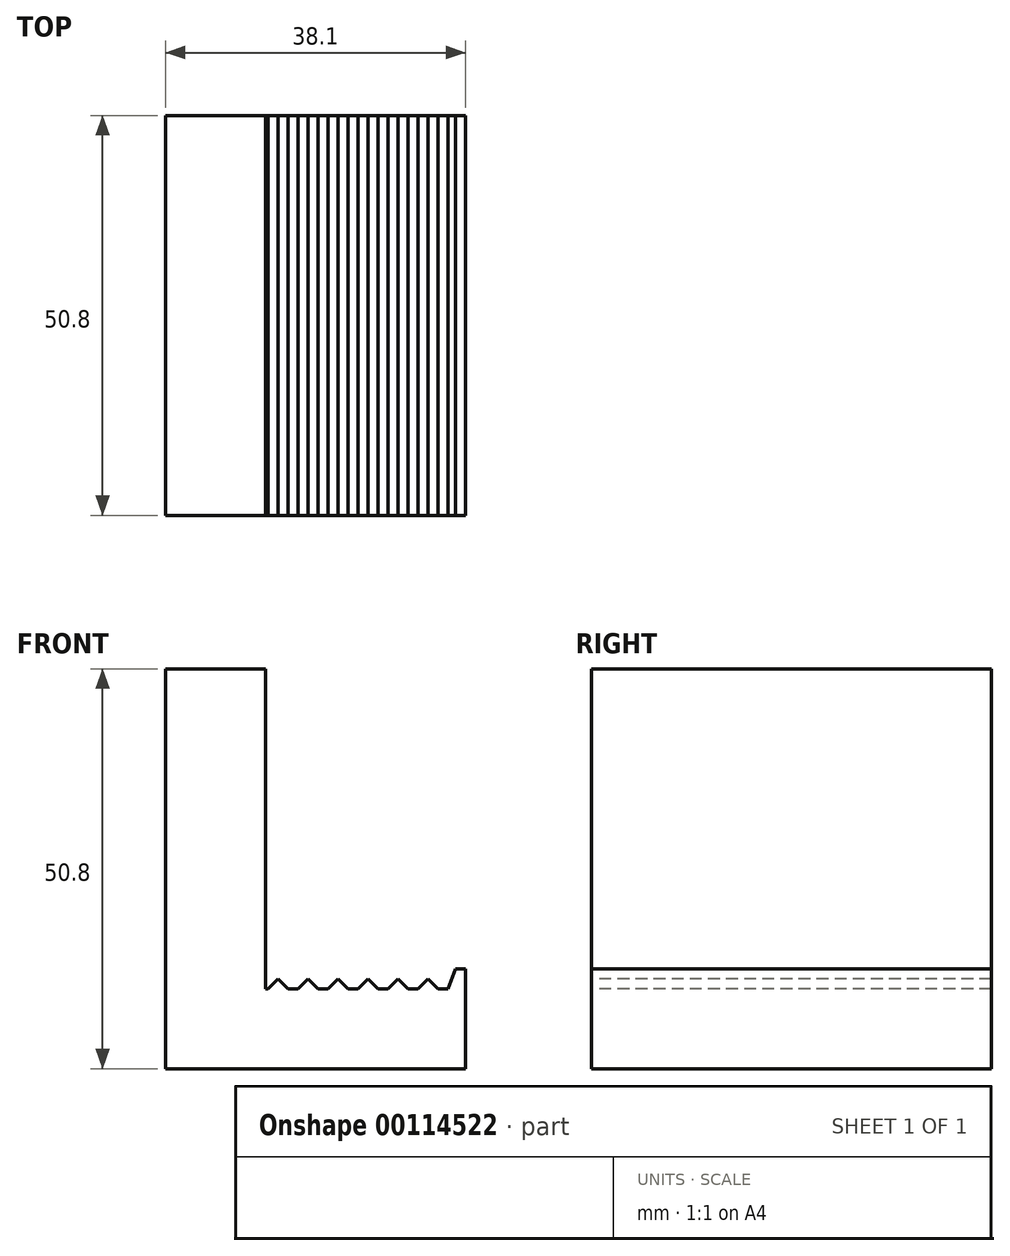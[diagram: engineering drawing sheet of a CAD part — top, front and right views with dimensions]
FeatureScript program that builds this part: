
annotation { "Feature Type Name" : "Feature", "Feature Type Description" : "" }
export const myFeature = defineFeature(function(context is Context, id is Id, definition is map)
    precondition{}
    {
        {
            var Q0;
            Q0=qCreatedBy(makeId("Front.planeOp"),FACE);
            var sketch = newSketch(context, id + "F0", { "sketchPlane" : qUnion([Q0])});
            skLineSegment(sketch, "E0", {"start": v(0, 0) * mm, "end": v(-38.1, 0) * mm});
            skLineSegment(sketch, "E1", {"start": v(-38.1, 0) * mm, "end": v(-38.1, 50.8) * mm});
            skLineSegment(sketch, "E2", {"start": v(-38.1, 50.8) * mm, "end": v(-25.4, 50.8) * mm});
            skLineSegment(sketch, "E3", {"start": v(-25.4, 50.8) * mm, "end": v(-25.4, 10.16) * mm});
            skLineSegment(sketch, "E4", {"start": v(0, 12.7) * mm, "end": v(0, 0) * mm});
            skLineSegment(sketch, "E5", {"start": v(0, 12.7) * mm, "end": v(-1.27, 12.7) * mm});
            skLineSegment(sketch, "E6", {"start": v(-1.27, 12.7) * mm, "end": v(-2.2, 10.16) * mm});
            skLineSegment(sketch, "E7", {"start": v(-2.2, 10.16) * mm, "end": v(-3.46, 10.16) * mm});
            skLineSegment(sketch, "E8", {"start": v(-3.46, 10.16) * mm, "end": v(-4.73, 11.43) * mm});
            skLineSegment(sketch, "E9", {"start": v(-6, 10.16) * mm, "end": v(-4.73, 11.43) * mm});
            skLineSegment(sketch, "E10.1.0.0", {"start": v(-6, 10.16) * mm, "end": v(-7.27, 10.16) * mm});
            skLineSegment(sketch, "E10.1.0.1", {"start": v(-7.27, 10.16) * mm, "end": v(-8.54, 11.43) * mm});
            skLineSegment(sketch, "E10.1.0.2", {"start": v(-9.81, 10.16) * mm, "end": v(-8.54, 11.43) * mm});
            skLineSegment(sketch, "E10.2.0.0", {"start": v(-9.81, 10.16) * mm, "end": v(-11.08, 10.16) * mm});
            skLineSegment(sketch, "E10.2.0.1", {"start": v(-11.08, 10.16) * mm, "end": v(-12.35, 11.43) * mm});
            skLineSegment(sketch, "E10.2.0.2", {"start": v(-13.62, 10.16) * mm, "end": v(-12.35, 11.43) * mm});
            skLineSegment(sketch, "E10.3.0.0", {"start": v(-13.62, 10.16) * mm, "end": v(-14.9, 10.16) * mm});
            skLineSegment(sketch, "E10.3.0.1", {"start": v(-14.9, 10.16) * mm, "end": v(-16.16, 11.43) * mm});
            skLineSegment(sketch, "E10.3.0.2", {"start": v(-17.43, 10.16) * mm, "end": v(-16.16, 11.43) * mm});
            skLineSegment(sketch, "E10.4.0.0", {"start": v(-17.43, 10.16) * mm, "end": v(-18.7, 10.16) * mm});
            skLineSegment(sketch, "E10.4.0.1", {"start": v(-18.7, 10.16) * mm, "end": v(-19.97, 11.43) * mm});
            skLineSegment(sketch, "E10.4.0.2", {"start": v(-21.24, 10.16) * mm, "end": v(-19.97, 11.43) * mm});
            skLineSegment(sketch, "E10.5.0.0", {"start": v(-21.24, 10.16) * mm, "end": v(-22.51, 10.16) * mm});
            skLineSegment(sketch, "E10.5.0.1", {"start": v(-22.51, 10.16) * mm, "end": v(-23.78, 11.43) * mm});
            skLineSegment(sketch, "E10.5.0.2", {"start": v(-25.05, 10.16) * mm, "end": v(-23.78, 11.43) * mm});
            skLineSegment(sketch, "E10.direction1", {"start": v(-6, 10.16) * mm, "end": v(-9.81, 10.16) * mm, "construction": true});
            skLineSegment(sketch, "E11", {"start": v(-25.05, 10.16) * mm, "end": v(-25.4, 10.16) * mm});
            skSolve(sketch);
        }
        {
            var Q0;
            Q0 = qSketchRegion(id + "F0", true);
            extrude(context, id + "F1", {"entities" : qUnion([Q0]), "oppositeDirection" : true, "depth" : 50.8 * mm});
        }
    });
